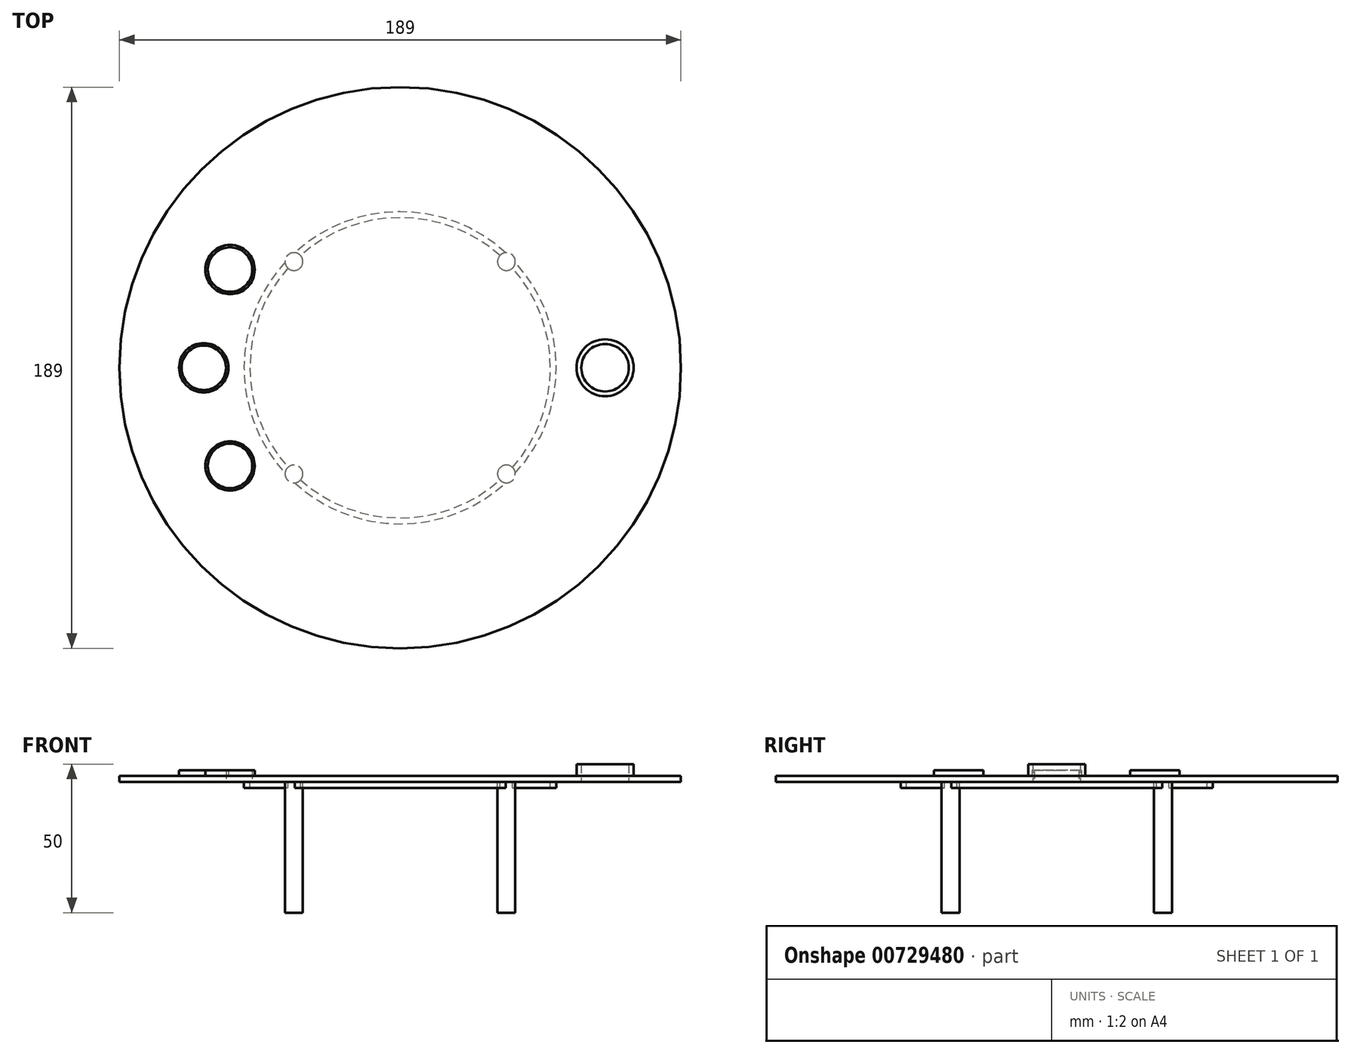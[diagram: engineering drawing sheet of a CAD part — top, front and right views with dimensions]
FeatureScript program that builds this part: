
annotation { "Feature Type Name" : "Feature", "Feature Type Description" : "" }
export const myFeature = defineFeature(function(context is Context, id is Id, definition is map)
    precondition{}
    {
        {
            var Q0;
            Q0=qCreatedBy(makeId("Top.planeOp"),FACE);
            var sketch = newSketch(context, id + "F0", { "sketchPlane" : qUnion([Q0])});
            skCircle(sketch, "E0", {"center": v(0, 0) * mm, "radius": 94.5 * mm});
            skPoint(sketch, "E1", {"position": v(-66.13, 0) * mm});
            skPoint(sketch, "E2", {"position": v(68.97, 0) * mm});
            skCircle(sketch, "E3", {"center": v(0, 0) * mm, "radius": 66.13 * mm, "construction": true});
            skLineSegment(sketch, "E4", {"start": v(0, 0) * mm, "end": v(-57.27, 33.06) * mm, "construction": true});
            skLineSegment(sketch, "E5", {"start": v(0, 0) * mm, "end": v(-57.27, -33.06) * mm, "construction": true});
            skCircle(sketch, "E6", {"center": v(-66.13, 0) * mm, "radius": 7.5 * mm});
            skCircle(sketch, "E7", {"center": v(-57.27, 33.06) * mm, "radius": 7.5 * mm});
            skCircle(sketch, "E8", {"center": v(-57.27, -33.06) * mm, "radius": 7.5 * mm});
            skCircle(sketch, "E9", {"center": v(68.97, 0) * mm, "radius": 8 * mm});
            skCircle(sketch, "E10.0", {"center": v(-57.27, 33.06) * mm, "radius": 8.3 * mm});
            skCircle(sketch, "E11.0", {"center": v(-66.13, 0) * mm, "radius": 8.3 * mm});
            skCircle(sketch, "E12.0", {"center": v(-57.27, -33.06) * mm, "radius": 8.3 * mm});
            skCircle(sketch, "E13", {"center": v(0, 0) * mm, "radius": 52.56 * mm});
            skCircle(sketch, "E14.0", {"center": v(0, 0) * mm, "radius": 50.56 * mm});
            skCircle(sketch, "E15.0", {"center": v(68.97, 0) * mm, "radius": 9.6 * mm});
            skLineSegment(sketch, "E16", {"start": v(0, 0) * mm, "end": v(-35.75, -35.75) * mm, "construction": true});
            skLineSegment(sketch, "E17", {"start": v(0, 0) * mm, "end": v(35.75, 35.75) * mm, "construction": true});
            skLineSegment(sketch, "E18", {"start": v(0, 0) * mm, "end": v(-35.75, 35.75) * mm, "construction": true});
            skLineSegment(sketch, "E19", {"start": v(0, 0) * mm, "end": v(35.75, -35.75) * mm, "construction": true});
            skCircle(sketch, "E20", {"center": v(-35.75, -35.75) * mm, "radius": 3 * mm});
            skCircle(sketch, "E21", {"center": v(35.75, -35.75) * mm, "radius": 3 * mm});
            skCircle(sketch, "E22", {"center": v(35.75, 35.75) * mm, "radius": 3 * mm});
            skCircle(sketch, "E23", {"center": v(-35.75, 35.75) * mm, "radius": 3 * mm});
            skSolve(sketch);
        }
        {
            var Q0;
            Q0=makeQuery(id+"F0.imprint","IMPRINT",FACE,{"disambiguationData":[TD([[makeQuery(id+"F0.imprint","IMPRINT",EDGE,{"derivedFrom":sQuery(id+"F0.wireOp",EDGE,"E0")}),1.0]])]});
            var Q1;
            {var subQ0=sQuery(id+"F0.wireOp",EDGE,"sIBmuizu-38tI-5obV-rzRC-FqeWtWb39AiS");var subQ1=sQuery(id+"F0.wireOp",EDGE,"E13");var subQ2=makeQuery(id+"F0.imprint","INTERSECT",VERTEX,{"disambiguationData":[OD(1.0)],"derivedFrom":[subQ1,subQ0]});Q1=makeQuery(id+"F0.imprint","IMPRINT",FACE,{"disambiguationData":[TD([[makeQuery(id+"F0.imprint","IMPRINT",EDGE,{"disambiguationData":[TD([[subQ2,-1.0]])],"derivedFrom":subQ1}),1.0]])]});}
            var Q2;
            {var subQ1=sQuery(id+"F0.wireOp",EDGE,"E14.0");var subQ9=sQuery(id+"F0.wireOp",EDGE,"sIBmuizu-38tI-5obV-rzRC-FqeWtWb39AiS");var subQ12=makeQuery(id+"F0.imprint","INTERSECT",VERTEX,{"disambiguationData":[OD(0.0)],"derivedFrom":[subQ1,subQ9]});Q2=makeQuery(id+"F0.imprint","IMPRINT",FACE,{"disambiguationData":[TD([[makeQuery(id+"F0.imprint","IMPRINT",EDGE,{"disambiguationData":[TD([[subQ12,1.0]])],"derivedFrom":subQ1}),1.0]])]});}
            var Q3;
            {var subQ0=sQuery(id+"F0.wireOp",EDGE,"sIBmuizu-38tI-5obV-rzRC-FqeWtWb39AiS");var subQ1=sQuery(id+"F0.wireOp",EDGE,"E13");var subQ2=makeQuery(id+"F0.imprint","INTERSECT",VERTEX,{"disambiguationData":[OD(0.0)],"derivedFrom":[subQ1,subQ0]});Q3=makeQuery(id+"F0.imprint","IMPRINT",FACE,{"disambiguationData":[TD([[makeQuery(id+"F0.imprint","IMPRINT",EDGE,{"disambiguationData":[TD([[subQ2,1.0]])],"derivedFrom":subQ1}),1.0]])]});}
            var Q4;
            {var subQ0=sQuery(id+"F0.wireOp",EDGE,"ZTHyCRkf-SgcX-OzZn-apjB-5VcU0MUPfGKK");var subQ1=sQuery(id+"F0.wireOp",EDGE,"E13");var subQ2=makeQuery(id+"F0.imprint","INTERSECT",VERTEX,{"disambiguationData":[OD(1.0)],"derivedFrom":[subQ1,subQ0]});Q4=makeQuery(id+"F0.imprint","IMPRINT",FACE,{"disambiguationData":[TD([[makeQuery(id+"F0.imprint","IMPRINT",EDGE,{"disambiguationData":[TD([[subQ2,-1.0]])],"derivedFrom":subQ1}),1.0]])]});}
            var Q5;
            {var subQ0=sQuery(id+"F0.wireOp",EDGE,"QBahTCmE-WSpw-ygaS-X5Gx-bdPXAw5LSlfZ");var subQ1=sQuery(id+"F0.wireOp",EDGE,"E13");var subQ2=makeQuery(id+"F0.imprint","INTERSECT",VERTEX,{"disambiguationData":[OD(1.0)],"derivedFrom":[subQ1,subQ0]});Q5=makeQuery(id+"F0.imprint","IMPRINT",FACE,{"disambiguationData":[TD([[makeQuery(id+"F0.imprint","IMPRINT",EDGE,{"disambiguationData":[TD([[subQ2,-1.0]])],"derivedFrom":subQ1}),1.0]])]});}
            var Q6;
            {var subQ0=sQuery(id+"F0.wireOp",EDGE,"E22");var subQ1=sQuery(id+"F0.wireOp",EDGE,"E14.0");var subQ5=makeQuery(id+"F0.imprint","INTERSECT",VERTEX,{"disambiguationData":[OD(0.0)],"derivedFrom":[subQ1,subQ0]});Q6=makeQuery(id+"F0.imprint","IMPRINT",FACE,{"disambiguationData":[TD([[makeQuery(id+"F0.imprint","IMPRINT",EDGE,{"disambiguationData":[TD([[subQ5,-1.0]])],"derivedFrom":subQ1}),1.0]])]});}
            var Q7;
            {var subQ0=sQuery(id+"F0.wireOp",EDGE,"E23");var subQ1=sQuery(id+"F0.wireOp",EDGE,"E13");var subQ2=makeQuery(id+"F0.imprint","INTERSECT",VERTEX,{"disambiguationData":[OD(1.0)],"derivedFrom":[subQ1,subQ0]});Q7=makeQuery(id+"F0.imprint","IMPRINT",FACE,{"disambiguationData":[TD([[makeQuery(id+"F0.imprint","IMPRINT",EDGE,{"disambiguationData":[TD([[subQ2,-1.0]])],"derivedFrom":subQ1}),1.0]])]});}
            var Q8;
            {var subQ0=sQuery(id+"F0.wireOp",EDGE,"E20");var subQ1=sQuery(id+"F0.wireOp",EDGE,"E13");var subQ2=makeQuery(id+"F0.imprint","INTERSECT",VERTEX,{"disambiguationData":[OD(1.0)],"derivedFrom":[subQ1,subQ0]});Q8=makeQuery(id+"F0.imprint","IMPRINT",FACE,{"disambiguationData":[TD([[makeQuery(id+"F0.imprint","IMPRINT",EDGE,{"disambiguationData":[TD([[subQ2,-1.0]])],"derivedFrom":subQ1}),1.0]])]});}
            var Q9;
            {var subQ0=sQuery(id+"F0.wireOp",EDGE,"E22");var subQ1=sQuery(id+"F0.wireOp",EDGE,"E13");var subQ2=makeQuery(id+"F0.imprint","INTERSECT",VERTEX,{"disambiguationData":[OD(1.0)],"derivedFrom":[subQ1,subQ0]});Q9=makeQuery(id+"F0.imprint","IMPRINT",FACE,{"disambiguationData":[TD([[makeQuery(id+"F0.imprint","IMPRINT",EDGE,{"disambiguationData":[TD([[subQ2,1.0]])],"derivedFrom":subQ1}),1.0]])]});}
            var Q10;
            {var subQ0=sQuery(id+"F0.wireOp",EDGE,"E22");var subQ1=sQuery(id+"F0.wireOp",EDGE,"E13");var subQ2=makeQuery(id+"F0.imprint","INTERSECT",VERTEX,{"disambiguationData":[OD(0.0)],"derivedFrom":[subQ1,subQ0]});Q10=makeQuery(id+"F0.imprint","IMPRINT",FACE,{"disambiguationData":[TD([[makeQuery(id+"F0.imprint","IMPRINT",EDGE,{"disambiguationData":[TD([[subQ2,-1.0]])],"derivedFrom":subQ1}),1.0]])]});}
            var Q11;
            {var subQ0=sQuery(id+"F0.wireOp",EDGE,"E21");var subQ1=sQuery(id+"F0.wireOp",EDGE,"E14.0");var subQ2=makeQuery(id+"F0.imprint","INTERSECT",VERTEX,{"disambiguationData":[OD(0.0)],"derivedFrom":[subQ1,subQ0]});Q11=makeQuery(id+"F0.imprint","IMPRINT",FACE,{"disambiguationData":[TD([[makeQuery(id+"F0.imprint","IMPRINT",EDGE,{"disambiguationData":[TD([[subQ2,-1.0]])],"derivedFrom":subQ1}),1.0]])]});}
            var Q12;
            {var subQ0=sQuery(id+"F0.wireOp",EDGE,"E21");var subQ1=sQuery(id+"F0.wireOp",EDGE,"E13");var subQ2=makeQuery(id+"F0.imprint","INTERSECT",VERTEX,{"disambiguationData":[OD(0.0)],"derivedFrom":[subQ1,subQ0]});Q12=makeQuery(id+"F0.imprint","IMPRINT",FACE,{"disambiguationData":[TD([[makeQuery(id+"F0.imprint","IMPRINT",EDGE,{"disambiguationData":[TD([[subQ2,-1.0]])],"derivedFrom":subQ1}),1.0]])]});}
            var Q13;
            {var subQ0=sQuery(id+"F0.wireOp",EDGE,"E21");var subQ1=sQuery(id+"F0.wireOp",EDGE,"E13");var subQ2=makeQuery(id+"F0.imprint","INTERSECT",VERTEX,{"disambiguationData":[OD(0.0)],"derivedFrom":[subQ1,subQ0]});Q13=makeQuery(id+"F0.imprint","IMPRINT",FACE,{"disambiguationData":[TD([[makeQuery(id+"F0.imprint","IMPRINT",EDGE,{"disambiguationData":[TD([[subQ2,-1.0]])],"derivedFrom":subQ1}),-1.0]])]});}
            var Q14;
            {var subQ0=sQuery(id+"F0.wireOp",EDGE,"E22");var subQ1=sQuery(id+"F0.wireOp",EDGE,"E14.0");var subQ2=makeQuery(id+"F0.imprint","INTERSECT",VERTEX,{"disambiguationData":[OD(0.0)],"derivedFrom":[subQ1,subQ0]});Q14=makeQuery(id+"F0.imprint","IMPRINT",FACE,{"disambiguationData":[TD([[makeQuery(id+"F0.imprint","IMPRINT",EDGE,{"disambiguationData":[TD([[subQ2,1.0]])],"derivedFrom":subQ1}),1.0]])]});}
            var Q15;
            {var subQ0=sQuery(id+"F0.wireOp",EDGE,"E22");var subQ1=sQuery(id+"F0.wireOp",EDGE,"E13");var subQ2=makeQuery(id+"F0.imprint","INTERSECT",VERTEX,{"disambiguationData":[OD(0.0)],"derivedFrom":[subQ1,subQ0]});Q15=makeQuery(id+"F0.imprint","IMPRINT",FACE,{"disambiguationData":[TD([[makeQuery(id+"F0.imprint","IMPRINT",EDGE,{"disambiguationData":[TD([[subQ2,1.0]])],"derivedFrom":subQ1}),1.0]])]});}
            var Q16;
            {var subQ0=sQuery(id+"F0.wireOp",EDGE,"E22");var subQ1=sQuery(id+"F0.wireOp",EDGE,"E13");var subQ2=makeQuery(id+"F0.imprint","INTERSECT",VERTEX,{"disambiguationData":[OD(0.0)],"derivedFrom":[subQ1,subQ0]});Q16=makeQuery(id+"F0.imprint","IMPRINT",FACE,{"disambiguationData":[TD([[makeQuery(id+"F0.imprint","IMPRINT",EDGE,{"disambiguationData":[TD([[subQ2,1.0]])],"derivedFrom":subQ1}),-1.0]])]});}
            var Q17;
            {var subQ0=sQuery(id+"F0.wireOp",EDGE,"E23");var subQ1=sQuery(id+"F0.wireOp",EDGE,"E13");var subQ2=makeQuery(id+"F0.imprint","INTERSECT",VERTEX,{"disambiguationData":[OD(0.0)],"derivedFrom":[subQ1,subQ0]});Q17=makeQuery(id+"F0.imprint","IMPRINT",FACE,{"disambiguationData":[TD([[makeQuery(id+"F0.imprint","IMPRINT",EDGE,{"disambiguationData":[TD([[subQ2,-1.0]])],"derivedFrom":subQ1}),-1.0]])]});}
            var Q18;
            {var subQ0=sQuery(id+"F0.wireOp",EDGE,"E23");var subQ1=sQuery(id+"F0.wireOp",EDGE,"E13");var subQ2=makeQuery(id+"F0.imprint","INTERSECT",VERTEX,{"disambiguationData":[OD(0.0)],"derivedFrom":[subQ1,subQ0]});Q18=makeQuery(id+"F0.imprint","IMPRINT",FACE,{"disambiguationData":[TD([[makeQuery(id+"F0.imprint","IMPRINT",EDGE,{"disambiguationData":[TD([[subQ2,-1.0]])],"derivedFrom":subQ1}),1.0]])]});}
            var Q19;
            {var subQ0=sQuery(id+"F0.wireOp",EDGE,"E23");var subQ1=sQuery(id+"F0.wireOp",EDGE,"E14.0");var subQ2=makeQuery(id+"F0.imprint","INTERSECT",VERTEX,{"disambiguationData":[OD(0.0)],"derivedFrom":[subQ1,subQ0]});Q19=makeQuery(id+"F0.imprint","IMPRINT",FACE,{"disambiguationData":[TD([[makeQuery(id+"F0.imprint","IMPRINT",EDGE,{"disambiguationData":[TD([[subQ2,-1.0]])],"derivedFrom":subQ1}),1.0]])]});}
            var Q20;
            {var subQ0=sQuery(id+"F0.wireOp",EDGE,"E20");var subQ1=sQuery(id+"F0.wireOp",EDGE,"E13");var subQ2=makeQuery(id+"F0.imprint","INTERSECT",VERTEX,{"disambiguationData":[OD(0.0)],"derivedFrom":[subQ1,subQ0]});Q20=makeQuery(id+"F0.imprint","IMPRINT",FACE,{"disambiguationData":[TD([[makeQuery(id+"F0.imprint","IMPRINT",EDGE,{"disambiguationData":[TD([[subQ2,-1.0]])],"derivedFrom":subQ1}),-1.0]])]});}
            var Q21;
            {var subQ0=sQuery(id+"F0.wireOp",EDGE,"E20");var subQ1=sQuery(id+"F0.wireOp",EDGE,"E13");var subQ2=makeQuery(id+"F0.imprint","INTERSECT",VERTEX,{"disambiguationData":[OD(0.0)],"derivedFrom":[subQ1,subQ0]});Q21=makeQuery(id+"F0.imprint","IMPRINT",FACE,{"disambiguationData":[TD([[makeQuery(id+"F0.imprint","IMPRINT",EDGE,{"disambiguationData":[TD([[subQ2,-1.0]])],"derivedFrom":subQ1}),1.0]])]});}
            var Q22;
            {var subQ0=sQuery(id+"F0.wireOp",EDGE,"E20");var subQ1=sQuery(id+"F0.wireOp",EDGE,"E14.0");var subQ2=makeQuery(id+"F0.imprint","INTERSECT",VERTEX,{"disambiguationData":[OD(0.0)],"derivedFrom":[subQ1,subQ0]});Q22=makeQuery(id+"F0.imprint","IMPRINT",FACE,{"disambiguationData":[TD([[makeQuery(id+"F0.imprint","IMPRINT",EDGE,{"disambiguationData":[TD([[subQ2,-1.0]])],"derivedFrom":subQ1}),1.0]])]});}
            extrude(context, id + "F1", {"entities" : qUnion([Q0, Q1, Q2, Q3, Q4, Q5, Q6, Q7, Q8, Q9, Q10, Q11, Q12, Q13, Q14, Q15, Q16, Q17, Q18, Q19, Q20, Q21, Q22]), "depth" : 2 * mm, "offsetDistance" : 25 * mm});
        }
        {
            var Q0;
            Q0=makeQuery(id+"F0.imprint","IMPRINT",FACE,{"disambiguationData":[TD([[makeQuery(id+"F0.imprint","IMPRINT",EDGE,{"derivedFrom":sQuery(id+"F0.wireOp",EDGE,"E7")}),-1.0]])]});
            var Q1;
            Q1=makeQuery(id+"F0.imprint","IMPRINT",FACE,{"disambiguationData":[TD([[makeQuery(id+"F0.imprint","IMPRINT",EDGE,{"derivedFrom":sQuery(id+"F0.wireOp",EDGE,"E6")}),-1.0]])]});
            var Q2;
            Q2=makeQuery(id+"F0.imprint","IMPRINT",FACE,{"disambiguationData":[TD([[makeQuery(id+"F0.imprint","IMPRINT",EDGE,{"derivedFrom":sQuery(id+"F0.wireOp",EDGE,"E8")}),-1.0]])]});
            extrude(context, id + "F2", {"entities" : qUnion([Q0, Q1, Q2]), "operationType" : NewBodyOperationType.ADD, "depth" : 4 * mm, "offsetDistance" : 25 * mm});
        }
        {
            var Q0;
            {var subQ0=sQuery(id+"F0.wireOp",EDGE,"E23");var subQ1=sQuery(id+"F0.wireOp",EDGE,"E13");var subQ2=makeQuery(id+"F0.imprint","INTERSECT",VERTEX,{"disambiguationData":[OD(1.0)],"derivedFrom":[subQ1,subQ0]});Q0=makeQuery(id+"F0.imprint","IMPRINT",FACE,{"disambiguationData":[TD([[makeQuery(id+"F0.imprint","IMPRINT",EDGE,{"disambiguationData":[TD([[subQ2,-1.0]])],"derivedFrom":subQ1}),1.0]])]});}
            var Q1;
            {var subQ0=sQuery(id+"F0.wireOp",EDGE,"E20");var subQ1=sQuery(id+"F0.wireOp",EDGE,"E13");var subQ2=makeQuery(id+"F0.imprint","INTERSECT",VERTEX,{"disambiguationData":[OD(1.0)],"derivedFrom":[subQ1,subQ0]});Q1=makeQuery(id+"F0.imprint","IMPRINT",FACE,{"disambiguationData":[TD([[makeQuery(id+"F0.imprint","IMPRINT",EDGE,{"disambiguationData":[TD([[subQ2,-1.0]])],"derivedFrom":subQ1}),1.0]])]});}
            var Q2;
            {var subQ0=sQuery(id+"F0.wireOp",EDGE,"E22");var subQ1=sQuery(id+"F0.wireOp",EDGE,"E13");var subQ2=makeQuery(id+"F0.imprint","INTERSECT",VERTEX,{"disambiguationData":[OD(1.0)],"derivedFrom":[subQ1,subQ0]});Q2=makeQuery(id+"F0.imprint","IMPRINT",FACE,{"disambiguationData":[TD([[makeQuery(id+"F0.imprint","IMPRINT",EDGE,{"disambiguationData":[TD([[subQ2,1.0]])],"derivedFrom":subQ1}),1.0]])]});}
            var Q3;
            {var subQ0=sQuery(id+"F0.wireOp",EDGE,"E22");var subQ1=sQuery(id+"F0.wireOp",EDGE,"E13");var subQ2=makeQuery(id+"F0.imprint","INTERSECT",VERTEX,{"disambiguationData":[OD(0.0)],"derivedFrom":[subQ1,subQ0]});Q3=makeQuery(id+"F0.imprint","IMPRINT",FACE,{"disambiguationData":[TD([[makeQuery(id+"F0.imprint","IMPRINT",EDGE,{"disambiguationData":[TD([[subQ2,-1.0]])],"derivedFrom":subQ1}),1.0]])]});}
            extrude(context, id + "F3", {"entities" : qUnion([Q0, Q1, Q2, Q3]), "operationType" : NewBodyOperationType.ADD, "oppositeDirection" : true, "depth" : 2 * mm, "offsetDistance" : 25 * mm});
        }
        {
            var Q0;
            Q0=makeQuery(id+"F0.imprint","IMPRINT",FACE,{"disambiguationData":[TD([[makeQuery(id+"F0.imprint","IMPRINT",EDGE,{"derivedFrom":sQuery(id+"F0.wireOp",EDGE,"E9")}),-1.0]])]});
            extrude(context, id + "F4", {"entities" : qUnion([Q0]), "operationType" : NewBodyOperationType.ADD, "depth" : 6 * mm, "offsetDistance" : 25 * mm});
        }
        {
            var Q0;
            {var subQ0=sQuery(id+"F0.wireOp",EDGE,"E20");var subQ1=sQuery(id+"F0.wireOp",EDGE,"E14.0");var subQ2=makeQuery(id+"F0.imprint","INTERSECT",VERTEX,{"disambiguationData":[OD(0.0)],"derivedFrom":[subQ1,subQ0]});Q0=makeQuery(id+"F0.imprint","IMPRINT",FACE,{"disambiguationData":[TD([[makeQuery(id+"F0.imprint","IMPRINT",EDGE,{"disambiguationData":[TD([[subQ2,-1.0]])],"derivedFrom":subQ1}),1.0]])]});}
            var Q1;
            {var subQ0=sQuery(id+"F0.wireOp",EDGE,"E20");var subQ1=sQuery(id+"F0.wireOp",EDGE,"E13");var subQ2=makeQuery(id+"F0.imprint","INTERSECT",VERTEX,{"disambiguationData":[OD(0.0)],"derivedFrom":[subQ1,subQ0]});Q1=makeQuery(id+"F0.imprint","IMPRINT",FACE,{"disambiguationData":[TD([[makeQuery(id+"F0.imprint","IMPRINT",EDGE,{"disambiguationData":[TD([[subQ2,-1.0]])],"derivedFrom":subQ1}),1.0]])]});}
            var Q2;
            {var subQ0=sQuery(id+"F0.wireOp",EDGE,"E20");var subQ1=sQuery(id+"F0.wireOp",EDGE,"E13");var subQ2=makeQuery(id+"F0.imprint","INTERSECT",VERTEX,{"disambiguationData":[OD(0.0)],"derivedFrom":[subQ1,subQ0]});Q2=makeQuery(id+"F0.imprint","IMPRINT",FACE,{"disambiguationData":[TD([[makeQuery(id+"F0.imprint","IMPRINT",EDGE,{"disambiguationData":[TD([[subQ2,-1.0]])],"derivedFrom":subQ1}),-1.0]])]});}
            var Q3;
            {var subQ0=sQuery(id+"F0.wireOp",EDGE,"E23");var subQ1=sQuery(id+"F0.wireOp",EDGE,"E14.0");var subQ2=makeQuery(id+"F0.imprint","INTERSECT",VERTEX,{"disambiguationData":[OD(0.0)],"derivedFrom":[subQ1,subQ0]});Q3=makeQuery(id+"F0.imprint","IMPRINT",FACE,{"disambiguationData":[TD([[makeQuery(id+"F0.imprint","IMPRINT",EDGE,{"disambiguationData":[TD([[subQ2,-1.0]])],"derivedFrom":subQ1}),1.0]])]});}
            var Q4;
            {var subQ0=sQuery(id+"F0.wireOp",EDGE,"E23");var subQ1=sQuery(id+"F0.wireOp",EDGE,"E13");var subQ2=makeQuery(id+"F0.imprint","INTERSECT",VERTEX,{"disambiguationData":[OD(0.0)],"derivedFrom":[subQ1,subQ0]});Q4=makeQuery(id+"F0.imprint","IMPRINT",FACE,{"disambiguationData":[TD([[makeQuery(id+"F0.imprint","IMPRINT",EDGE,{"disambiguationData":[TD([[subQ2,-1.0]])],"derivedFrom":subQ1}),1.0]])]});}
            var Q5;
            {var subQ0=sQuery(id+"F0.wireOp",EDGE,"E23");var subQ1=sQuery(id+"F0.wireOp",EDGE,"E13");var subQ2=makeQuery(id+"F0.imprint","INTERSECT",VERTEX,{"disambiguationData":[OD(0.0)],"derivedFrom":[subQ1,subQ0]});Q5=makeQuery(id+"F0.imprint","IMPRINT",FACE,{"disambiguationData":[TD([[makeQuery(id+"F0.imprint","IMPRINT",EDGE,{"disambiguationData":[TD([[subQ2,-1.0]])],"derivedFrom":subQ1}),-1.0]])]});}
            var Q6;
            {var subQ0=sQuery(id+"F0.wireOp",EDGE,"E22");var subQ1=sQuery(id+"F0.wireOp",EDGE,"E13");var subQ2=makeQuery(id+"F0.imprint","INTERSECT",VERTEX,{"disambiguationData":[OD(0.0)],"derivedFrom":[subQ1,subQ0]});Q6=makeQuery(id+"F0.imprint","IMPRINT",FACE,{"disambiguationData":[TD([[makeQuery(id+"F0.imprint","IMPRINT",EDGE,{"disambiguationData":[TD([[subQ2,1.0]])],"derivedFrom":subQ1}),-1.0]])]});}
            var Q7;
            {var subQ0=sQuery(id+"F0.wireOp",EDGE,"E22");var subQ1=sQuery(id+"F0.wireOp",EDGE,"E13");var subQ2=makeQuery(id+"F0.imprint","INTERSECT",VERTEX,{"disambiguationData":[OD(0.0)],"derivedFrom":[subQ1,subQ0]});Q7=makeQuery(id+"F0.imprint","IMPRINT",FACE,{"disambiguationData":[TD([[makeQuery(id+"F0.imprint","IMPRINT",EDGE,{"disambiguationData":[TD([[subQ2,1.0]])],"derivedFrom":subQ1}),1.0]])]});}
            var Q8;
            {var subQ0=sQuery(id+"F0.wireOp",EDGE,"E22");var subQ1=sQuery(id+"F0.wireOp",EDGE,"E14.0");var subQ2=makeQuery(id+"F0.imprint","INTERSECT",VERTEX,{"disambiguationData":[OD(0.0)],"derivedFrom":[subQ1,subQ0]});Q8=makeQuery(id+"F0.imprint","IMPRINT",FACE,{"disambiguationData":[TD([[makeQuery(id+"F0.imprint","IMPRINT",EDGE,{"disambiguationData":[TD([[subQ2,1.0]])],"derivedFrom":subQ1}),1.0]])]});}
            var Q9;
            {var subQ0=sQuery(id+"F0.wireOp",EDGE,"E21");var subQ1=sQuery(id+"F0.wireOp",EDGE,"E13");var subQ2=makeQuery(id+"F0.imprint","INTERSECT",VERTEX,{"disambiguationData":[OD(0.0)],"derivedFrom":[subQ1,subQ0]});Q9=makeQuery(id+"F0.imprint","IMPRINT",FACE,{"disambiguationData":[TD([[makeQuery(id+"F0.imprint","IMPRINT",EDGE,{"disambiguationData":[TD([[subQ2,-1.0]])],"derivedFrom":subQ1}),-1.0]])]});}
            var Q10;
            {var subQ0=sQuery(id+"F0.wireOp",EDGE,"E21");var subQ1=sQuery(id+"F0.wireOp",EDGE,"E13");var subQ2=makeQuery(id+"F0.imprint","INTERSECT",VERTEX,{"disambiguationData":[OD(0.0)],"derivedFrom":[subQ1,subQ0]});Q10=makeQuery(id+"F0.imprint","IMPRINT",FACE,{"disambiguationData":[TD([[makeQuery(id+"F0.imprint","IMPRINT",EDGE,{"disambiguationData":[TD([[subQ2,-1.0]])],"derivedFrom":subQ1}),1.0]])]});}
            var Q11;
            {var subQ0=sQuery(id+"F0.wireOp",EDGE,"E21");var subQ1=sQuery(id+"F0.wireOp",EDGE,"E14.0");var subQ2=makeQuery(id+"F0.imprint","INTERSECT",VERTEX,{"disambiguationData":[OD(0.0)],"derivedFrom":[subQ1,subQ0]});Q11=makeQuery(id+"F0.imprint","IMPRINT",FACE,{"disambiguationData":[TD([[makeQuery(id+"F0.imprint","IMPRINT",EDGE,{"disambiguationData":[TD([[subQ2,-1.0]])],"derivedFrom":subQ1}),1.0]])]});}
            extrude(context, id + "F5", {"entities" : qUnion([Q0, Q1, Q2, Q3, Q4, Q5, Q6, Q7, Q8, Q9, Q10, Q11]), "operationType" : NewBodyOperationType.ADD, "oppositeDirection" : true, "depth" : 44 * mm, "offsetDistance" : 25 * mm});
        }
    });
